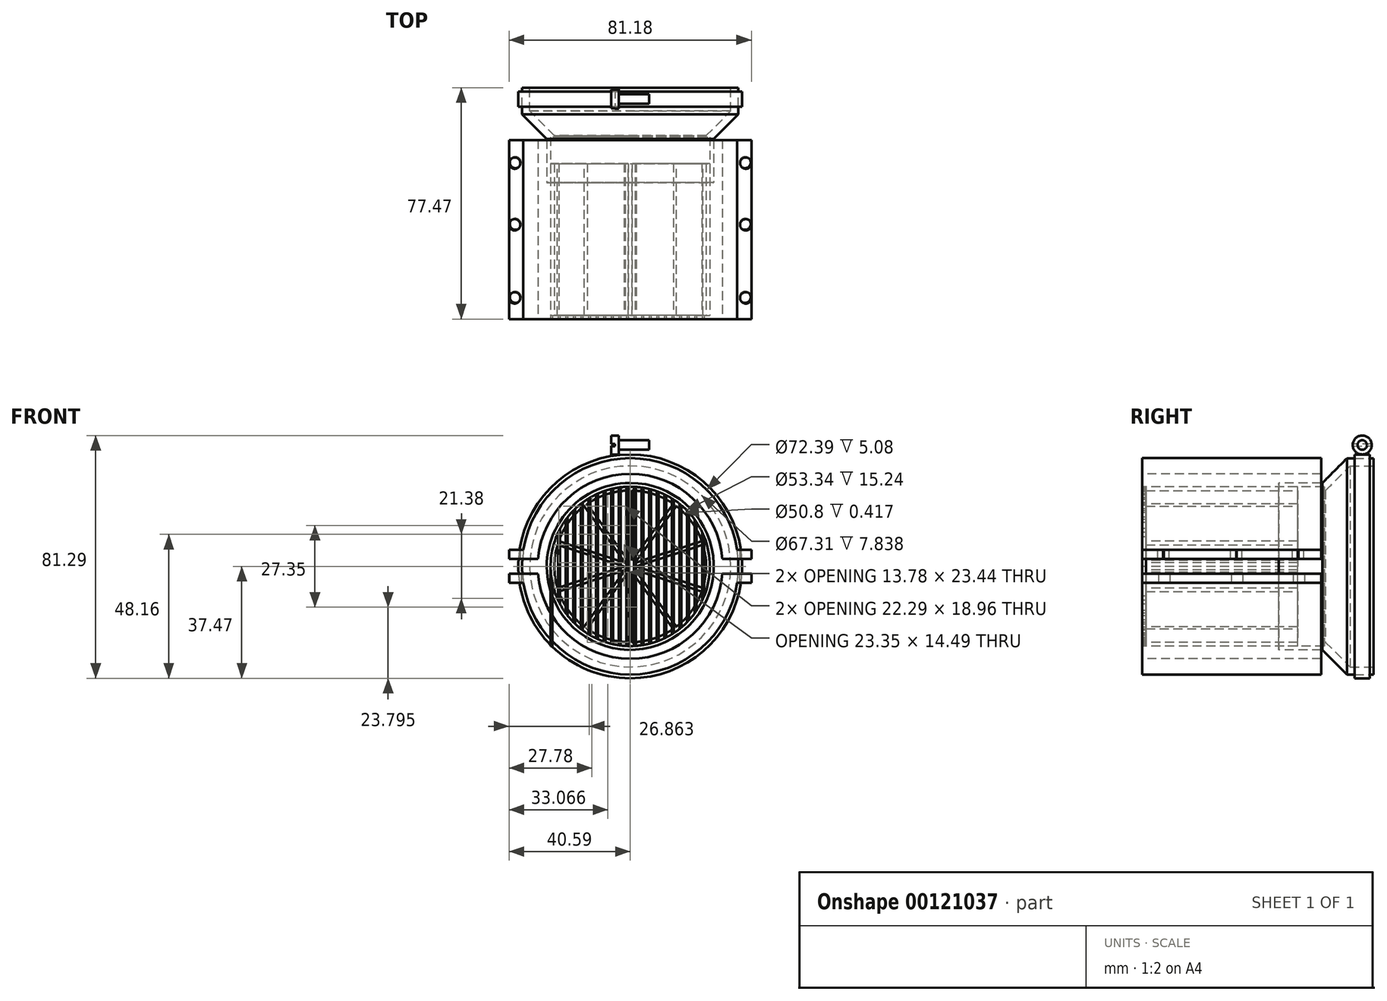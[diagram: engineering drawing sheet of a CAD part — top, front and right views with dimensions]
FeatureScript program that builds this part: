
annotation { "Feature Type Name" : "Feature", "Feature Type Description" : "" }
export const myFeature = defineFeature(function(context is Context, id is Id, definition is map)
    precondition{}
    {
        {
            var Q0;
            Q0=qCreatedBy(makeId("Front.planeOp"),FACE);
            var sketch = newSketch(context, id + "F0", { "sketchPlane" : qUnion([Q0])});
            skPoint(sketch, "E0", {"position": v(0.63, 25.4) * mm});
            skPoint(sketch, "E1", {"position": v(-0.64, 25.4) * mm});
            skLineSegment(sketch, "E2", {"start": v(-0.64, 25.4) * mm, "end": v(0.63, 25.4) * mm});
            skLineSegment(sketch, "E3", {"start": v(0.63, 25.4) * mm, "end": v(0.63, 0.46) * mm});
            skLineSegment(sketch, "E4", {"start": v(-0.64, 25.4) * mm, "end": v(-0.64, 0.2) * mm});
            skPoint(sketch, "E5.1.0", {"position": v(-14.42, 20.92) * mm});
            skLineSegment(sketch, "E5.1.1", {"start": v(-14.42, 20.92) * mm, "end": v(-0.64, 1.95) * mm});
            skLineSegment(sketch, "E5.1.2", {"start": v(-15.44, 20.18) * mm, "end": v(-1.66, 1.2) * mm});
            skPoint(sketch, "E5.1.3", {"position": v(-15.44, 20.18) * mm});
            skLineSegment(sketch, "E5.1.4", {"start": v(-15.44, 20.18) * mm, "end": v(-14.42, 20.92) * mm});
            skPoint(sketch, "E5.2.0", {"position": v(-23.96, 8.45) * mm});
            skLineSegment(sketch, "E5.2.1", {"start": v(-23.96, 8.45) * mm, "end": v(-1.66, 1.2) * mm});
            skLineSegment(sketch, "E5.2.2", {"start": v(-24.35, 7.25) * mm, "end": v(-2.05, 0) * mm});
            skPoint(sketch, "E5.2.3", {"position": v(-24.35, 7.25) * mm});
            skLineSegment(sketch, "E5.2.4", {"start": v(-24.35, 7.25) * mm, "end": v(-23.96, 8.45) * mm});
            skPoint(sketch, "E5.3.0", {"position": v(-24.35, -7.25) * mm});
            skLineSegment(sketch, "E5.3.1", {"start": v(-24.35, -7.25) * mm, "end": v(-2.05, 0) * mm});
            skLineSegment(sketch, "E5.3.2", {"start": v(-23.96, -8.45) * mm, "end": v(-1.66, -1.2) * mm});
            skPoint(sketch, "E5.3.3", {"position": v(-23.96, -8.45) * mm});
            skLineSegment(sketch, "E5.3.4", {"start": v(-23.96, -8.45) * mm, "end": v(-24.35, -7.25) * mm});
            skPoint(sketch, "E5.4.0", {"position": v(-15.44, -20.18) * mm});
            skLineSegment(sketch, "E5.4.1", {"start": v(-15.44, -20.18) * mm, "end": v(-1.66, -1.2) * mm});
            skLineSegment(sketch, "E5.4.2", {"start": v(-14.42, -20.92) * mm, "end": v(-0.63, -1.95) * mm});
            skPoint(sketch, "E5.4.3", {"position": v(-14.42, -20.92) * mm});
            skLineSegment(sketch, "E5.4.4", {"start": v(-14.42, -20.92) * mm, "end": v(-15.44, -20.18) * mm});
            skPoint(sketch, "E5.5.0", {"position": v(-0.64, -25.4) * mm});
            skLineSegment(sketch, "E5.5.1", {"start": v(-0.64, -25.4) * mm, "end": v(-0.63, -1.95) * mm});
            skLineSegment(sketch, "E5.5.2", {"start": v(0.63, -25.4) * mm, "end": v(0.64, -1.95) * mm});
            skPoint(sketch, "E5.5.3", {"position": v(0.63, -25.4) * mm});
            skLineSegment(sketch, "E5.5.4", {"start": v(0.63, -25.4) * mm, "end": v(-0.64, -25.4) * mm});
            skPoint(sketch, "E5.6.0", {"position": v(14.42, -20.92) * mm});
            skLineSegment(sketch, "E5.6.1", {"start": v(14.42, -20.92) * mm, "end": v(0.63, -1.95) * mm});
            skLineSegment(sketch, "E5.6.2", {"start": v(15.44, -20.18) * mm, "end": v(1.66, -1.2) * mm});
            skPoint(sketch, "E5.6.3", {"position": v(15.44, -20.18) * mm});
            skLineSegment(sketch, "E5.6.4", {"start": v(15.44, -20.18) * mm, "end": v(14.42, -20.92) * mm});
            skPoint(sketch, "E5.7.0", {"position": v(23.96, -8.45) * mm});
            skLineSegment(sketch, "E5.7.1", {"start": v(23.96, -8.45) * mm, "end": v(1.66, -1.2) * mm});
            skLineSegment(sketch, "E5.7.2", {"start": v(24.35, -7.25) * mm, "end": v(2.05, 0) * mm});
            skPoint(sketch, "E5.7.3", {"position": v(24.35, -7.25) * mm});
            skLineSegment(sketch, "E5.7.4", {"start": v(24.35, -7.25) * mm, "end": v(23.96, -8.45) * mm});
            skPoint(sketch, "E5.8.0", {"position": v(24.35, 7.25) * mm});
            skLineSegment(sketch, "E5.8.1", {"start": v(24.35, 7.25) * mm, "end": v(2.05, 0) * mm});
            skLineSegment(sketch, "E5.8.2", {"start": v(23.96, 8.45) * mm, "end": v(1.66, 1.2) * mm});
            skPoint(sketch, "E5.8.3", {"position": v(23.96, 8.45) * mm});
            skLineSegment(sketch, "E5.8.4", {"start": v(23.96, 8.45) * mm, "end": v(24.35, 7.25) * mm});
            skPoint(sketch, "E5.9.0", {"position": v(15.44, 20.18) * mm});
            skLineSegment(sketch, "E5.9.1", {"start": v(15.44, 20.18) * mm, "end": v(1.66, 1.2) * mm});
            skLineSegment(sketch, "E5.9.2", {"start": v(14.42, 20.92) * mm, "end": v(0.63, 1.95) * mm});
            skPoint(sketch, "E5.9.3", {"position": v(14.42, 20.92) * mm});
            skLineSegment(sketch, "E5.9.4", {"start": v(14.42, 20.92) * mm, "end": v(15.44, 20.18) * mm});
            skPoint(sketch, "E5.center", {"position": v(0, 0) * mm});
            skLineSegment(sketch, "E6.trimOffspring", {"start": v(0.63, 0.87) * mm, "end": v(0.24, 0.75) * mm});
            skLineSegment(sketch, "E7.trimOffspring", {"start": v(1.03, 0.33) * mm, "end": v(0.78, 0) * mm});
            skLineSegment(sketch, "E8.trimOffspring", {"start": v(1.03, 0.33) * mm, "end": v(0.63, 0.46) * mm});
            skLineSegment(sketch, "E9.trimOffspring", {"start": v(1.03, -0.33) * mm, "end": v(0.64, -0.46) * mm});
            skLineSegment(sketch, "E10.trimOffspring", {"start": v(1.03, -0.33) * mm, "end": v(0.78, 0) * mm});
            skLineSegment(sketch, "E11.trimOffspring", {"start": v(0.64, -0.87) * mm, "end": v(0.24, -0.75) * mm});
            skLineSegment(sketch, "E12.trimOffspring", {"start": v(0.64, -0.87) * mm, "end": v(0.64, -0.46) * mm});
            skLineSegment(sketch, "E13.trimOffspring", {"start": v(0, -1.08) * mm, "end": v(-0.24, -0.75) * mm});
            skLineSegment(sketch, "E14.trimOffspring", {"start": v(0, -1.08) * mm, "end": v(0.24, -0.75) * mm});
            skLineSegment(sketch, "E15.trimOffspring", {"start": v(-0.63, -0.87) * mm, "end": v(-0.63, -0.46) * mm});
            skLineSegment(sketch, "E16.trimOffspring", {"start": v(-0.63, -0.87) * mm, "end": v(-0.24, -0.75) * mm});
            skLineSegment(sketch, "E17.trimOffspring", {"start": v(-1.03, -0.33) * mm, "end": v(-0.78, 0) * mm});
            skLineSegment(sketch, "E18.trimOffspring", {"start": v(-1.03, -0.33) * mm, "end": v(-0.63, -0.46) * mm});
            skLineSegment(sketch, "E19.trimOffspring", {"start": v(-1.03, 0.33) * mm, "end": v(-0.2, 0.6) * mm});
            skLineSegment(sketch, "E20.trimOffspring", {"start": v(-1.03, 0.33) * mm, "end": v(-0.78, 0) * mm});
            skPoint(sketch, "E21.orphan", {"position": v(-0.64, 0) * mm});
            skPoint(sketch, "E22.orphan", {"position": v(0.63, 0) * mm});
            skPoint(sketch, "E23.orphan", {"position": v(0.64, 0) * mm});
            skPoint(sketch, "E24.orphan", {"position": v(0.51, -0.37) * mm});
            skPoint(sketch, "E25.orphan", {"position": v(-0.2, -0.6) * mm});
            skPoint(sketch, "E26.orphan", {"position": v(0.2, -0.6) * mm});
            skPoint(sketch, "E27.orphan", {"position": v(0.51, 0.37) * mm});
            skPoint(sketch, "E28.orphan", {"position": v(-0.51, 0.37) * mm});
            skPoint(sketch, "E29.orphan", {"position": v(-0.51, -0.37) * mm});
            skPoint(sketch, "E30.orphan", {"position": v(-0.2, 0.6) * mm});
            skSolve(sketch);
        }
        {
            var Q0;
            {var subQ6=sQuery(id+"F0.wireOp",EDGE,"E2");Q0=makeQuery(id+"F0.imprint","IMPRINT",FACE,{"disambiguationData":[TD([[makeQuery(id+"F0.imprint","IMPRINT",EDGE,{"derivedFrom":subQ6}),-1.0]])]});}
            var Q1;
            {var subQ1=sQuery(id+"F0.wireOp",EDGE,"E5.1.1");Q1=makeQuery(id+"F0.imprint","IMPRINT",FACE,{"disambiguationData":[TD([[makeQuery(id+"F0.imprint","IMPRINT",EDGE,{"derivedFrom":subQ1}),-1.0]])]});}
            extrude(context, id + "F1", {"entities" : qUnion([Q0, Q1]), "oppositeDirection" : true, "depth" : 50.8 * mm});
        }
        {
            var Q0;
            Q0=qCreatedBy(makeId("Front.planeOp"),FACE);
            var sketch = newSketch(context, id + "F2", { "sketchPlane" : qUnion([Q0])});
            skCircle(sketch, "E31", {"center": v(0, 0) * mm, "radius": 25.4 * mm});
            skCircle(sketch, "E32", {"center": v(0, 0) * mm, "radius": 26.67 * mm});
            skSolve(sketch);
        }
        {
            var Q0;
            Q0=makeQuery(id+"F2.imprint","IMPRINT",FACE,{"disambiguationData":[TD([[makeQuery(id+"F2.imprint","IMPRINT",EDGE,{"derivedFrom":sQuery(id+"F2.wireOp",EDGE,"E31")}),-1.0]])]});
            extrude(context, id + "F3", {"entities" : qUnion([Q0]), "operationType" : NewBodyOperationType.ADD, "oppositeDirection" : true, "depth" : 50.8 * mm});
        }
        {
            var Q0;
            Q0=makeQuery(id+"F3.boolean.opBoolean","MERGE",FACE,{"derivedFrom":[makeQuery(id+"F1.opExtrude","CAP_FACE",FACE,{"disambiguationData":[OSD([sQuery(id+"F0.wireOp",EDGE,"E2"),sQuery(id+"F0.wireOp",EDGE,"E3"),sQuery(id+"F0.wireOp",EDGE,"E4"),sQuery(id+"F0.wireOp",EDGE,"E5.1.1"),sQuery(id+"F0.wireOp",EDGE,"E5.1.2"),sQuery(id+"F0.wireOp",EDGE,"E5.1.4"),sQuery(id+"F0.wireOp",EDGE,"E5.2.1"),sQuery(id+"F0.wireOp",EDGE,"E5.2.2"),sQuery(id+"F0.wireOp",EDGE,"E5.2.4"),sQuery(id+"F0.wireOp",EDGE,"E5.3.1"),sQuery(id+"F0.wireOp",EDGE,"E5.3.2"),sQuery(id+"F0.wireOp",EDGE,"E5.3.4"),sQuery(id+"F0.wireOp",EDGE,"E5.4.1"),sQuery(id+"F0.wireOp",EDGE,"E5.4.2"),sQuery(id+"F0.wireOp",EDGE,"E5.4.4"),sQuery(id+"F0.wireOp",EDGE,"E5.5.1"),sQuery(id+"F0.wireOp",EDGE,"E5.5.2"),sQuery(id+"F0.wireOp",EDGE,"E5.5.4"),sQuery(id+"F0.wireOp",EDGE,"E5.6.1"),sQuery(id+"F0.wireOp",EDGE,"E5.6.2"),sQuery(id+"F0.wireOp",EDGE,"E5.6.4"),sQuery(id+"F0.wireOp",EDGE,"E5.7.1"),sQuery(id+"F0.wireOp",EDGE,"E5.7.2"),sQuery(id+"F0.wireOp",EDGE,"E5.7.4"),sQuery(id+"F0.wireOp",EDGE,"E5.8.1"),sQuery(id+"F0.wireOp",EDGE,"E5.8.2"),sQuery(id+"F0.wireOp",EDGE,"E5.8.4"),sQuery(id+"F0.wireOp",EDGE,"E5.9.1"),sQuery(id+"F0.wireOp",EDGE,"E5.9.2"),sQuery(id+"F0.wireOp",EDGE,"E5.9.4")])],"isStart":false}),makeQuery(id+"F3.opExtrude","CAP_FACE",FACE,{"disambiguationData":[OSD([sQuery(id+"F2.wireOp",EDGE,"E31"),sQuery(id+"F2.wireOp",EDGE,"E32")])],"isStart":false})]});
            var sketch = newSketch(context, id + "F4", { "sketchPlane" : qUnion([Q0])});
            skCircle(sketch, "E33", {"center": v(0, 0) * mm, "radius": 26.67 * mm});
            skCircle(sketch, "E34", {"center": v(0, 0) * mm, "radius": 27.94 * mm});
            skSolve(sketch);
        }
        {
            var Q0;
            Q0=makeQuery(id+"F4.imprint","IMPRINT",FACE,{"disambiguationData":[TD([[makeQuery(id+"F4.imprint","IMPRINT",EDGE,{"derivedFrom":sQuery(id+"F4.wireOp",EDGE,"E33")}),-1.0]])]});
            cPlane(context, id + "F5", {"entities" : qUnion([Q0]), "cplaneType" : CPlaneType.OFFSET, "offset" : 25.4 * mm, "width" : 152.4 * mm, "height" : 152.4 * mm});
        }
        {
            var Q0;
            Q0=qCreatedBy(id+"F5.planeOp",FACE);
            var sketch = newSketch(context, id + "F6", { "sketchPlane" : qUnion([Q0])});
            skCircle(sketch, "E35", {"center": v(0, 0) * mm, "radius": 36.2 * mm});
            skSolve(sketch);
        }
        {
            var Q0;
            Q0=makeQuery(id+"F4.imprint","IMPRINT",FACE,{"disambiguationData":[TD([[makeQuery(id+"F4.imprint","IMPRINT",EDGE,{"derivedFrom":sQuery(id+"F4.wireOp",EDGE,"E33")}),1.0]])]});
            extrude(context, id + "F7", {"entities" : qUnion([Q0]), "endBound" : BoundingType.SYMMETRIC, "depth" : 12.7 * mm});
        }
        {
            var Q0;
            Q0=makeQuery(id+"F6.imprint","IMPRINT",FACE,{"disambiguationData":[TD([[makeQuery(id+"F6.imprint","IMPRINT",EDGE,{"derivedFrom":sQuery(id+"F6.wireOp",EDGE,"E35")}),1.0]])]});
            extrude(context, id + "F8", {"entities" : qUnion([Q0]), "operationType" : NewBodyOperationType.ADD, "oppositeDirection" : true, "depth" : 19.05 * mm});
        }
        {
            var Q0;
            Q0=makeQuery(id+"F8.opExtrude","CAP_EDGE",EDGE,{"disambiguationData":[OSD([sQuery(id+"F6.wireOp",EDGE,"E35")])],"isStart":false});
            chamfer(context, id + "F9", {"entities" : qUnion([Q0]), "width" : 10.16 * mm, "tangentPropagation" : true});
        }
        {
            var Q0;
            Q0=makeQuery(id+"F8.opExtrude","CAP_FACE",FACE,{"disambiguationData":[OSD([sQuery(id+"F6.wireOp",EDGE,"E35")])],"isStart":true});
            shell(context, id + "F10", {"entities" : qUnion([Q0]), "thickness" : 2.54 * mm});
        }
        {
            var Q0;
            Q0=makeQuery(id+"F6.imprint","IMPRINT",FACE,{"disambiguationData":[TD([[makeQuery(id+"F6.imprint","IMPRINT",EDGE,{"derivedFrom":sQuery(id+"F6.wireOp",EDGE,"E35")}),1.0]])]});
            cPlane(context, id + "F11", {"entities" : qUnion([Q0]), "cplaneType" : CPlaneType.OFFSET, "offset" : 16.5 * mm, "oppositeDirection" : true, "width" : 152.4 * mm, "height" : 152.4 * mm});
        }
        {
            var Q0;
            Q0=qCreatedBy(id+"F11.planeOp",FACE);
            var sketch = newSketch(context, id + "F12", { "sketchPlane" : qUnion([Q0])});
            skCircle(sketch, "E36", {"center": v(0, 0) * mm, "radius": 26.67 * mm});
            skSolve(sketch);
        }
        {
            var Q0;
            Q0 = qSketchRegion(id + "F12", true);
            extrude(context, id + "F13", {"entities" : qUnion([Q0]), "operationType" : NewBodyOperationType.REMOVE, "oppositeDirection" : true, "depth" : 2.54 * mm});
        }
        {
            var Q0;
            Q0=makeQuery(id+"F3.boolean.opBoolean","MERGE",FACE,{"derivedFrom":[makeQuery(id+"F1.opExtrude","CAP_FACE",FACE,{"disambiguationData":[OSD([sQuery(id+"F0.wireOp",EDGE,"E2"),sQuery(id+"F0.wireOp",EDGE,"E3"),sQuery(id+"F0.wireOp",EDGE,"E4"),sQuery(id+"F0.wireOp",EDGE,"E5.1.1"),sQuery(id+"F0.wireOp",EDGE,"E5.1.2"),sQuery(id+"F0.wireOp",EDGE,"E5.1.4"),sQuery(id+"F0.wireOp",EDGE,"E5.2.1"),sQuery(id+"F0.wireOp",EDGE,"E5.2.2"),sQuery(id+"F0.wireOp",EDGE,"E5.2.4"),sQuery(id+"F0.wireOp",EDGE,"E5.3.1"),sQuery(id+"F0.wireOp",EDGE,"E5.3.2"),sQuery(id+"F0.wireOp",EDGE,"E5.3.4"),sQuery(id+"F0.wireOp",EDGE,"E5.4.1"),sQuery(id+"F0.wireOp",EDGE,"E5.4.2"),sQuery(id+"F0.wireOp",EDGE,"E5.4.4"),sQuery(id+"F0.wireOp",EDGE,"E5.5.1"),sQuery(id+"F0.wireOp",EDGE,"E5.5.2"),sQuery(id+"F0.wireOp",EDGE,"E5.5.4"),sQuery(id+"F0.wireOp",EDGE,"E5.6.1"),sQuery(id+"F0.wireOp",EDGE,"E5.6.2"),sQuery(id+"F0.wireOp",EDGE,"E5.6.4"),sQuery(id+"F0.wireOp",EDGE,"E5.7.1"),sQuery(id+"F0.wireOp",EDGE,"E5.7.2"),sQuery(id+"F0.wireOp",EDGE,"E5.7.4"),sQuery(id+"F0.wireOp",EDGE,"E5.8.1"),sQuery(id+"F0.wireOp",EDGE,"E5.8.2"),sQuery(id+"F0.wireOp",EDGE,"E5.8.4"),sQuery(id+"F0.wireOp",EDGE,"E5.9.1"),sQuery(id+"F0.wireOp",EDGE,"E5.9.2"),sQuery(id+"F0.wireOp",EDGE,"E5.9.4")])],"isStart":true}),makeQuery(id+"F3.opExtrude","CAP_FACE",FACE,{"disambiguationData":[OSD([sQuery(id+"F2.wireOp",EDGE,"E31"),sQuery(id+"F2.wireOp",EDGE,"E32")])],"isStart":true})]});
            cPlane(context, id + "F14", {"entities" : qUnion([Q0]), "cplaneType" : CPlaneType.OFFSET, "offset" : 1.27 * mm, "width" : 152.4 * mm, "height" : 152.4 * mm});
        }
        {
            var Q0;
            Q0=qCreatedBy(id+"F14.planeOp",FACE);
            var sketch = newSketch(context, id + "F15", { "sketchPlane" : qUnion([Q0])});
            skLineSegment(sketch, "E37.bottom", {"start": v(-26.67, 26.67) * mm, "end": v(26.67, 26.67) * mm});
            skLineSegment(sketch, "E37.top", {"start": v(-26.67, -26.67) * mm, "end": v(26.67, -26.67) * mm});
            skLineSegment(sketch, "E37.left", {"start": v(-26.67, 26.67) * mm, "end": v(-26.67, -26.67) * mm});
            skLineSegment(sketch, "E37.right", {"start": v(26.67, 26.67) * mm, "end": v(26.67, -26.67) * mm});
            skPoint(sketch, "E37.middle", {"position": v(0, 0) * mm});
            skPoint(sketch, "E38", {"position": v(-26.03, 26.67) * mm});
            skLineSegment(sketch, "E39", {"start": v(-26.03, 26.67) * mm, "end": v(-26.04, -26.67) * mm});
            skLineSegment(sketch, "E40.MirrorCS", {"start": v(-25.4, 26.67) * mm, "end": v(-25.4, -26.67) * mm});
            skLineSegment(sketch, "E41.MirrorCS", {"start": v(-24.77, 26.67) * mm, "end": v(-24.77, -26.67) * mm});
            skLineSegment(sketch, "E42.MirrorCS", {"start": v(-24.13, 26.67) * mm, "end": v(-24.13, -26.67) * mm});
            skLineSegment(sketch, "E43.MirrorCS", {"start": v(-23.5, 26.67) * mm, "end": v(-23.5, -26.67) * mm});
            skLineSegment(sketch, "E44.MirrorCS", {"start": v(-22.86, 26.67) * mm, "end": v(-22.86, -26.67) * mm});
            skLineSegment(sketch, "E45.MirrorCS", {"start": v(-22.23, 26.67) * mm, "end": v(-22.23, -26.67) * mm});
            skLineSegment(sketch, "E46.MirrorCS", {"start": v(-21.59, 26.67) * mm, "end": v(-21.59, -26.67) * mm});
            skLineSegment(sketch, "E47.MirrorCS", {"start": v(-20.96, 26.67) * mm, "end": v(-20.96, -26.67) * mm});
            skLineSegment(sketch, "E48.MirrorCS", {"start": v(-20.32, 26.67) * mm, "end": v(-20.32, -26.67) * mm});
            skLineSegment(sketch, "E49.MirrorCS", {"start": v(-19.68, 26.67) * mm, "end": v(-19.69, -26.67) * mm});
            skLineSegment(sketch, "E50.MirrorCS", {"start": v(-19.05, 26.67) * mm, "end": v(-19.05, -26.67) * mm});
            skLineSegment(sketch, "E51.MirrorCS", {"start": v(-18.42, 26.67) * mm, "end": v(-18.42, -26.67) * mm});
            skLineSegment(sketch, "E52.MirrorCS", {"start": v(-17.78, 26.67) * mm, "end": v(-17.78, -26.67) * mm});
            skLineSegment(sketch, "E53.MirrorCS", {"start": v(-17.15, 26.67) * mm, "end": v(-17.15, -26.67) * mm});
            skLineSegment(sketch, "E54.MirrorCS", {"start": v(-16.5, 26.67) * mm, "end": v(-16.51, -26.67) * mm});
            skLineSegment(sketch, "E55.MirrorCS", {"start": v(-15.87, 26.67) * mm, "end": v(-15.88, -26.67) * mm});
            skLineSegment(sketch, "E56.MirrorCS", {"start": v(-15.24, 26.67) * mm, "end": v(-15.24, -26.67) * mm});
            skLineSegment(sketch, "E57.MirrorCS", {"start": v(-14.6, 26.67) * mm, "end": v(-14.6, -26.67) * mm});
            skLineSegment(sketch, "E58.MirrorCS", {"start": v(-13.33, 26.67) * mm, "end": v(-13.34, -26.67) * mm});
            skLineSegment(sketch, "E59.MirrorCS", {"start": v(-13.97, 26.67) * mm, "end": v(-13.97, -26.67) * mm});
            skLineSegment(sketch, "E60.MirrorCS", {"start": v(-12.7, 26.67) * mm, "end": v(-12.7, -26.67) * mm});
            skLineSegment(sketch, "E61.MirrorCS", {"start": v(-12.07, 26.67) * mm, "end": v(-12.07, -26.67) * mm});
            skLineSegment(sketch, "E62.MirrorCS", {"start": v(-11.43, 26.67) * mm, "end": v(-11.43, -26.67) * mm});
            skLineSegment(sketch, "E63.MirrorCS", {"start": v(-10.8, 26.67) * mm, "end": v(-10.8, -26.67) * mm});
            skLineSegment(sketch, "E64.MirrorCS", {"start": v(-10.16, 26.67) * mm, "end": v(-10.16, -26.67) * mm});
            skLineSegment(sketch, "E65.MirrorCS", {"start": v(-9.52, 26.67) * mm, "end": v(-9.52, -26.67) * mm});
            skLineSegment(sketch, "E66.MirrorCS", {"start": v(-8.9, 26.67) * mm, "end": v(-8.9, -26.67) * mm});
            skLineSegment(sketch, "E67.MirrorCS", {"start": v(-8.26, 26.67) * mm, "end": v(-8.26, -26.67) * mm});
            skLineSegment(sketch, "E68.MirrorCS", {"start": v(-6.98, 26.67) * mm, "end": v(-6.99, -26.67) * mm});
            skLineSegment(sketch, "E69.MirrorCS", {"start": v(-7.62, 26.67) * mm, "end": v(-7.62, -26.67) * mm});
            skLineSegment(sketch, "E70.MirrorCS", {"start": v(-6.35, 26.67) * mm, "end": v(-6.35, -26.67) * mm});
            skLineSegment(sketch, "E71.MirrorCS", {"start": v(-5.71, 26.67) * mm, "end": v(-5.71, -26.67) * mm});
            skLineSegment(sketch, "E72.MirrorCS", {"start": v(-5.08, 26.67) * mm, "end": v(-5.08, -26.67) * mm});
            skLineSegment(sketch, "E73.MirrorCS", {"start": v(-4.45, 26.67) * mm, "end": v(-4.45, -26.67) * mm});
            skLineSegment(sketch, "E74.MirrorCS", {"start": v(-3.81, 26.67) * mm, "end": v(-3.81, -26.67) * mm});
            skLineSegment(sketch, "E75.MirrorCS", {"start": v(-3.18, 26.67) * mm, "end": v(-3.18, -26.67) * mm});
            skLineSegment(sketch, "E76.MirrorCS", {"start": v(-2.54, 26.67) * mm, "end": v(-2.54, -26.67) * mm});
            skLineSegment(sketch, "E77.MirrorCS", {"start": v(-1.9, 26.67) * mm, "end": v(-1.9, -26.67) * mm});
            skLineSegment(sketch, "E78.MirrorCS", {"start": v(-1.27, 26.67) * mm, "end": v(-1.27, -26.67) * mm});
            skLineSegment(sketch, "E79.MirrorCS", {"start": v(-0.64, 26.67) * mm, "end": v(-0.64, -26.67) * mm});
            skLineSegment(sketch, "E80.MirrorCS", {"start": v(0, 26.67) * mm, "end": v(0, -26.67) * mm});
            skCircle(sketch, "E81", {"center": v(0, 0) * mm, "radius": 26.67 * mm});
            skSolve(sketch);
        }
        {
            var Q0;
            {var subQ0=sQuery(id+"F15.wireOp",EDGE,"E81");var subQ1=sQuery(id+"F15.wireOp",EDGE,"E39");var subQ2=makeQuery(id+"F15.imprint","INTERSECT",VERTEX,{"disambiguationData":[OD(0.0)],"derivedFrom":[subQ1,subQ0]});Q0=makeQuery(id+"F15.imprint","IMPRINT",FACE,{"disambiguationData":[TD([[makeQuery(id+"F15.imprint","IMPRINT",EDGE,{"disambiguationData":[TD([[subQ2,-1.0]])],"derivedFrom":subQ1}),-1.0]])]});}
            var Q1;
            {var subQ0=sQuery(id+"F15.wireOp",EDGE,"E81");var subQ1=sQuery(id+"F15.wireOp",EDGE,"E42.MirrorCS");var subQ2=makeQuery(id+"F15.imprint","INTERSECT",VERTEX,{"disambiguationData":[OD(0.0)],"derivedFrom":[subQ1,subQ0]});Q1=makeQuery(id+"F15.imprint","IMPRINT",FACE,{"disambiguationData":[TD([[makeQuery(id+"F15.imprint","IMPRINT",EDGE,{"disambiguationData":[TD([[subQ2,-1.0]])],"derivedFrom":subQ1}),1.0]])]});}
            var Q2;
            {var subQ0=sQuery(id+"F15.wireOp",EDGE,"E81");var subQ1=sQuery(id+"F15.wireOp",EDGE,"E46.MirrorCS");var subQ2=makeQuery(id+"F15.imprint","INTERSECT",VERTEX,{"disambiguationData":[OD(0.0)],"derivedFrom":[subQ1,subQ0]});Q2=makeQuery(id+"F15.imprint","IMPRINT",FACE,{"disambiguationData":[TD([[makeQuery(id+"F15.imprint","IMPRINT",EDGE,{"disambiguationData":[TD([[subQ2,-1.0]])],"derivedFrom":subQ1}),1.0]])]});}
            var Q3;
            {var subQ0=sQuery(id+"F15.wireOp",EDGE,"E81");var subQ1=sQuery(id+"F15.wireOp",EDGE,"E50.MirrorCS");var subQ2=makeQuery(id+"F15.imprint","INTERSECT",VERTEX,{"disambiguationData":[OD(0.0)],"derivedFrom":[subQ1,subQ0]});Q3=makeQuery(id+"F15.imprint","IMPRINT",FACE,{"disambiguationData":[TD([[makeQuery(id+"F15.imprint","IMPRINT",EDGE,{"disambiguationData":[TD([[subQ2,-1.0]])],"derivedFrom":subQ1}),1.0]])]});}
            var Q4;
            {var subQ0=sQuery(id+"F15.wireOp",EDGE,"E81");var subQ1=sQuery(id+"F15.wireOp",EDGE,"E54.MirrorCS");var subQ2=makeQuery(id+"F15.imprint","INTERSECT",VERTEX,{"disambiguationData":[OD(0.0)],"derivedFrom":[subQ1,subQ0]});Q4=makeQuery(id+"F15.imprint","IMPRINT",FACE,{"disambiguationData":[TD([[makeQuery(id+"F15.imprint","IMPRINT",EDGE,{"disambiguationData":[TD([[subQ2,-1.0]])],"derivedFrom":subQ1}),1.0]])]});}
            var Q5;
            {var subQ0=sQuery(id+"F15.wireOp",EDGE,"E81");var subQ1=sQuery(id+"F15.wireOp",EDGE,"E58.MirrorCS");var subQ2=makeQuery(id+"F15.imprint","INTERSECT",VERTEX,{"disambiguationData":[OD(0.0)],"derivedFrom":[subQ1,subQ0]});Q5=makeQuery(id+"F15.imprint","IMPRINT",FACE,{"disambiguationData":[TD([[makeQuery(id+"F15.imprint","IMPRINT",EDGE,{"disambiguationData":[TD([[subQ2,-1.0]])],"derivedFrom":subQ1}),-1.0]])]});}
            var Q6;
            {var subQ0=sQuery(id+"F15.wireOp",EDGE,"E81");var subQ1=sQuery(id+"F15.wireOp",EDGE,"E62.MirrorCS");var subQ2=makeQuery(id+"F15.imprint","INTERSECT",VERTEX,{"disambiguationData":[OD(0.0)],"derivedFrom":[subQ1,subQ0]});Q6=makeQuery(id+"F15.imprint","IMPRINT",FACE,{"disambiguationData":[TD([[makeQuery(id+"F15.imprint","IMPRINT",EDGE,{"disambiguationData":[TD([[subQ2,-1.0]])],"derivedFrom":subQ1}),1.0]])]});}
            var Q7;
            {var subQ0=sQuery(id+"F15.wireOp",EDGE,"E81");var subQ1=sQuery(id+"F15.wireOp",EDGE,"E66.MirrorCS");var subQ2=makeQuery(id+"F15.imprint","INTERSECT",VERTEX,{"disambiguationData":[OD(0.0)],"derivedFrom":[subQ1,subQ0]});Q7=makeQuery(id+"F15.imprint","IMPRINT",FACE,{"disambiguationData":[TD([[makeQuery(id+"F15.imprint","IMPRINT",EDGE,{"disambiguationData":[TD([[subQ2,-1.0]])],"derivedFrom":subQ1}),1.0]])]});}
            var Q8;
            {var subQ0=sQuery(id+"F15.wireOp",EDGE,"E81");var subQ1=sQuery(id+"F15.wireOp",EDGE,"E70.MirrorCS");var subQ2=makeQuery(id+"F15.imprint","INTERSECT",VERTEX,{"disambiguationData":[OD(0.0)],"derivedFrom":[subQ1,subQ0]});Q8=makeQuery(id+"F15.imprint","IMPRINT",FACE,{"disambiguationData":[TD([[makeQuery(id+"F15.imprint","IMPRINT",EDGE,{"disambiguationData":[TD([[subQ2,-1.0]])],"derivedFrom":subQ1}),1.0]])]});}
            var Q9;
            {var subQ0=sQuery(id+"F15.wireOp",EDGE,"E81");var subQ1=sQuery(id+"F15.wireOp",EDGE,"E74.MirrorCS");var subQ2=makeQuery(id+"F15.imprint","INTERSECT",VERTEX,{"disambiguationData":[OD(0.0)],"derivedFrom":[subQ1,subQ0]});Q9=makeQuery(id+"F15.imprint","IMPRINT",FACE,{"disambiguationData":[TD([[makeQuery(id+"F15.imprint","IMPRINT",EDGE,{"disambiguationData":[TD([[subQ2,-1.0]])],"derivedFrom":subQ1}),1.0]])]});}
            var Q10;
            {var subQ0=sQuery(id+"F15.wireOp",EDGE,"E81");var subQ1=sQuery(id+"F15.wireOp",EDGE,"E79.MirrorCS");var subQ2=makeQuery(id+"F15.imprint","INTERSECT",VERTEX,{"disambiguationData":[OD(0.0)],"derivedFrom":[subQ1,subQ0]});Q10=makeQuery(id+"F15.imprint","IMPRINT",FACE,{"disambiguationData":[TD([[makeQuery(id+"F15.imprint","IMPRINT",EDGE,{"disambiguationData":[TD([[subQ2,-1.0]])],"derivedFrom":subQ1}),-1.0]])]});}
            extrude(context, id + "F16", {"entities" : qUnion([Q0, Q1, Q2, Q3, Q4, Q5, Q6, Q7, Q8, Q9, Q10]), "oppositeDirection" : true, "depth" : 1.27 * mm});
        }
        {
            var Q0;
            Q0=qCreatedBy(id+"F14.planeOp",FACE);
            var sketch = newSketch(context, id + "F17", { "sketchPlane" : qUnion([Q0])});
            skLineSegment(sketch, "E82.bottom", {"start": v(-26.67, 26.67) * mm, "end": v(26.67, 26.67) * mm});
            skLineSegment(sketch, "E82.top", {"start": v(-26.67, -26.67) * mm, "end": v(26.67, -26.67) * mm});
            skLineSegment(sketch, "E82.left", {"start": v(-26.67, 26.67) * mm, "end": v(-26.67, -26.67) * mm});
            skLineSegment(sketch, "E82.right", {"start": v(26.67, 26.67) * mm, "end": v(26.67, -26.67) * mm});
            skPoint(sketch, "E82.middle", {"position": v(0, 0) * mm});
            skCircle(sketch, "E83", {"center": v(0, 0) * mm, "radius": 26.67 * mm});
            skPoint(sketch, "E84", {"position": v(0.63, 26.67) * mm});
            skLineSegment(sketch, "E85", {"start": v(0, 26.67) * mm, "end": v(0, -26.67) * mm});
            skLineSegment(sketch, "E86", {"start": v(0.63, 26.67) * mm, "end": v(0.63, -26.67) * mm});
            skLineSegment(sketch, "E87.MirrorCS", {"start": v(1.27, 26.67) * mm, "end": v(1.27, -26.67) * mm});
            skLineSegment(sketch, "E88.MirrorCS", {"start": v(1.9, 26.67) * mm, "end": v(1.9, -26.67) * mm});
            skLineSegment(sketch, "E89.MirrorCS", {"start": v(2.54, 26.67) * mm, "end": v(2.54, -26.67) * mm});
            skLineSegment(sketch, "E90.MirrorCS", {"start": v(3.17, 26.67) * mm, "end": v(3.17, -26.67) * mm});
            skLineSegment(sketch, "E91.MirrorCS", {"start": v(3.8, 26.67) * mm, "end": v(3.8, -26.67) * mm});
            skLineSegment(sketch, "E92.MirrorCS", {"start": v(4.44, 26.67) * mm, "end": v(4.44, -26.67) * mm});
            skLineSegment(sketch, "E93.MirrorCS", {"start": v(5.08, 26.67) * mm, "end": v(5.08, -26.67) * mm});
            skLineSegment(sketch, "E94.MirrorCS", {"start": v(5.71, 26.67) * mm, "end": v(5.71, -26.67) * mm});
            skLineSegment(sketch, "E95.MirrorCS", {"start": v(6.35, 26.67) * mm, "end": v(6.35, -26.67) * mm});
            skLineSegment(sketch, "E96.MirrorCS", {"start": v(6.98, 26.67) * mm, "end": v(6.98, -26.67) * mm});
            skLineSegment(sketch, "E97.MirrorCS", {"start": v(7.62, 26.67) * mm, "end": v(7.62, -26.67) * mm});
            skLineSegment(sketch, "E98.MirrorCS", {"start": v(8.25, 26.67) * mm, "end": v(8.25, -26.67) * mm});
            skLineSegment(sketch, "E99.MirrorCS", {"start": v(8.89, 26.67) * mm, "end": v(8.89, -26.67) * mm});
            skLineSegment(sketch, "E100.MirrorCS", {"start": v(9.53, 26.67) * mm, "end": v(9.52, -26.67) * mm});
            skLineSegment(sketch, "E101.MirrorCS", {"start": v(10.16, 26.67) * mm, "end": v(10.16, -26.67) * mm});
            skLineSegment(sketch, "E102.MirrorCS", {"start": v(10.8, 26.67) * mm, "end": v(10.8, -26.67) * mm});
            skLineSegment(sketch, "E103.MirrorCS", {"start": v(12.06, 26.67) * mm, "end": v(12.06, -26.67) * mm});
            skLineSegment(sketch, "E104.MirrorCS", {"start": v(12.7, 26.67) * mm, "end": v(12.7, -26.67) * mm});
            skLineSegment(sketch, "E105.MirrorCS", {"start": v(11.43, 26.67) * mm, "end": v(11.43, -26.67) * mm});
            skLineSegment(sketch, "E106.MirrorCS", {"start": v(13.33, 26.67) * mm, "end": v(13.33, -26.67) * mm});
            skLineSegment(sketch, "E107.MirrorCS", {"start": v(13.97, 26.67) * mm, "end": v(13.97, -26.67) * mm});
            skLineSegment(sketch, "E108.MirrorCS", {"start": v(14.6, 26.67) * mm, "end": v(14.6, -26.67) * mm});
            skLineSegment(sketch, "E109.MirrorCS", {"start": v(15.24, 26.67) * mm, "end": v(15.24, -26.67) * mm});
            skLineSegment(sketch, "E110.MirrorCS", {"start": v(15.87, 26.67) * mm, "end": v(15.87, -26.67) * mm});
            skLineSegment(sketch, "E111.MirrorCS", {"start": v(16.5, 26.67) * mm, "end": v(16.5, -26.67) * mm});
            skLineSegment(sketch, "E112.MirrorCS", {"start": v(17.14, 26.67) * mm, "end": v(17.14, -26.67) * mm});
            skLineSegment(sketch, "E113.MirrorCS", {"start": v(17.78, 26.67) * mm, "end": v(17.78, -26.67) * mm});
            skLineSegment(sketch, "E114.MirrorCS", {"start": v(18.41, 26.67) * mm, "end": v(18.41, -26.67) * mm});
            skLineSegment(sketch, "E115.MirrorCS", {"start": v(19.05, 26.67) * mm, "end": v(19.05, -26.67) * mm});
            skLineSegment(sketch, "E116.MirrorCS", {"start": v(19.68, 26.67) * mm, "end": v(19.68, -26.67) * mm});
            skLineSegment(sketch, "E117.MirrorCS", {"start": v(20.32, 26.67) * mm, "end": v(20.32, -26.67) * mm});
            skLineSegment(sketch, "E118.MirrorCS", {"start": v(20.95, 26.67) * mm, "end": v(20.95, -26.67) * mm});
            skLineSegment(sketch, "E119.MirrorCS", {"start": v(21.59, 26.67) * mm, "end": v(21.59, -26.67) * mm});
            skLineSegment(sketch, "E120.MirrorCS", {"start": v(22.22, 26.67) * mm, "end": v(22.22, -26.67) * mm});
            skLineSegment(sketch, "E121.MirrorCS", {"start": v(22.86, 26.67) * mm, "end": v(22.86, -26.67) * mm});
            skLineSegment(sketch, "E122.MirrorCS", {"start": v(23.5, 26.67) * mm, "end": v(23.5, -26.67) * mm});
            skLineSegment(sketch, "E123.MirrorCS", {"start": v(24.13, 26.67) * mm, "end": v(24.13, -26.67) * mm});
            skLineSegment(sketch, "E124.MirrorCS", {"start": v(24.77, 26.67) * mm, "end": v(24.77, -26.67) * mm});
            skLineSegment(sketch, "E125.MirrorCS", {"start": v(25.4, 26.67) * mm, "end": v(25.4, -26.67) * mm});
            skLineSegment(sketch, "E126.MirrorCS", {"start": v(26.03, 26.67) * mm, "end": v(26.03, -26.67) * mm});
            skSolve(sketch);
        }
        {
            var Q0;
            {var subQ0=sQuery(id+"F17.wireOp",EDGE,"E88.MirrorCS");var subQ1=sQuery(id+"F17.wireOp",EDGE,"E83");var subQ2=makeQuery(id+"F17.imprint","INTERSECT",VERTEX,{"disambiguationData":[OD(0.0)],"derivedFrom":[subQ1,subQ0]});Q0=makeQuery(id+"F17.imprint","IMPRINT",FACE,{"disambiguationData":[TD([[makeQuery(id+"F17.imprint","IMPRINT",EDGE,{"disambiguationData":[TD([[subQ2,-1.0]])],"derivedFrom":subQ1}),1.0]])]});}
            var Q1;
            {var subQ0=sQuery(id+"F17.wireOp",EDGE,"E92.MirrorCS");var subQ1=sQuery(id+"F17.wireOp",EDGE,"E83");var subQ2=makeQuery(id+"F17.imprint","INTERSECT",VERTEX,{"disambiguationData":[OD(0.0)],"derivedFrom":[subQ1,subQ0]});Q1=makeQuery(id+"F17.imprint","IMPRINT",FACE,{"disambiguationData":[TD([[makeQuery(id+"F17.imprint","IMPRINT",EDGE,{"disambiguationData":[TD([[subQ2,-1.0]])],"derivedFrom":subQ1}),1.0]])]});}
            var Q2;
            {var subQ0=sQuery(id+"F17.wireOp",EDGE,"E96.MirrorCS");var subQ1=sQuery(id+"F17.wireOp",EDGE,"E83");var subQ2=makeQuery(id+"F17.imprint","INTERSECT",VERTEX,{"disambiguationData":[OD(0.0)],"derivedFrom":[subQ1,subQ0]});Q2=makeQuery(id+"F17.imprint","IMPRINT",FACE,{"disambiguationData":[TD([[makeQuery(id+"F17.imprint","IMPRINT",EDGE,{"disambiguationData":[TD([[subQ2,-1.0]])],"derivedFrom":subQ1}),1.0]])]});}
            var Q3;
            {var subQ0=sQuery(id+"F17.wireOp",EDGE,"E100.MirrorCS");var subQ1=sQuery(id+"F17.wireOp",EDGE,"E83");var subQ2=makeQuery(id+"F17.imprint","INTERSECT",VERTEX,{"disambiguationData":[OD(0.0)],"derivedFrom":[subQ1,subQ0]});Q3=makeQuery(id+"F17.imprint","IMPRINT",FACE,{"disambiguationData":[TD([[makeQuery(id+"F17.imprint","IMPRINT",EDGE,{"disambiguationData":[TD([[subQ2,-1.0]])],"derivedFrom":subQ1}),1.0]])]});}
            var Q4;
            {var subQ0=sQuery(id+"F17.wireOp",EDGE,"E103.MirrorCS");var subQ1=sQuery(id+"F17.wireOp",EDGE,"E83");var subQ2=makeQuery(id+"F17.imprint","INTERSECT",VERTEX,{"disambiguationData":[OD(0.0)],"derivedFrom":[subQ1,subQ0]});Q4=makeQuery(id+"F17.imprint","IMPRINT",FACE,{"disambiguationData":[TD([[makeQuery(id+"F17.imprint","IMPRINT",EDGE,{"disambiguationData":[TD([[subQ2,-1.0]])],"derivedFrom":subQ1}),1.0]])]});}
            var Q5;
            {var subQ0=sQuery(id+"F17.wireOp",EDGE,"E108.MirrorCS");var subQ1=sQuery(id+"F17.wireOp",EDGE,"E83");var subQ2=makeQuery(id+"F17.imprint","INTERSECT",VERTEX,{"disambiguationData":[OD(0.0)],"derivedFrom":[subQ1,subQ0]});Q5=makeQuery(id+"F17.imprint","IMPRINT",FACE,{"disambiguationData":[TD([[makeQuery(id+"F17.imprint","IMPRINT",EDGE,{"disambiguationData":[TD([[subQ2,-1.0]])],"derivedFrom":subQ1}),1.0]])]});}
            var Q6;
            {var subQ0=sQuery(id+"F17.wireOp",EDGE,"E112.MirrorCS");var subQ1=sQuery(id+"F17.wireOp",EDGE,"E83");var subQ2=makeQuery(id+"F17.imprint","INTERSECT",VERTEX,{"disambiguationData":[OD(0.0)],"derivedFrom":[subQ1,subQ0]});Q6=makeQuery(id+"F17.imprint","IMPRINT",FACE,{"disambiguationData":[TD([[makeQuery(id+"F17.imprint","IMPRINT",EDGE,{"disambiguationData":[TD([[subQ2,-1.0]])],"derivedFrom":subQ1}),1.0]])]});}
            var Q7;
            {var subQ0=sQuery(id+"F17.wireOp",EDGE,"E116.MirrorCS");var subQ1=sQuery(id+"F17.wireOp",EDGE,"E83");var subQ2=makeQuery(id+"F17.imprint","INTERSECT",VERTEX,{"disambiguationData":[OD(0.0)],"derivedFrom":[subQ1,subQ0]});Q7=makeQuery(id+"F17.imprint","IMPRINT",FACE,{"disambiguationData":[TD([[makeQuery(id+"F17.imprint","IMPRINT",EDGE,{"disambiguationData":[TD([[subQ2,-1.0]])],"derivedFrom":subQ1}),1.0]])]});}
            var Q8;
            {var subQ0=sQuery(id+"F17.wireOp",EDGE,"E120.MirrorCS");var subQ1=sQuery(id+"F17.wireOp",EDGE,"E83");var subQ2=makeQuery(id+"F17.imprint","INTERSECT",VERTEX,{"disambiguationData":[OD(0.0)],"derivedFrom":[subQ1,subQ0]});Q8=makeQuery(id+"F17.imprint","IMPRINT",FACE,{"disambiguationData":[TD([[makeQuery(id+"F17.imprint","IMPRINT",EDGE,{"disambiguationData":[TD([[subQ2,-1.0]])],"derivedFrom":subQ1}),1.0]])]});}
            var Q9;
            {var subQ0=sQuery(id+"F17.wireOp",EDGE,"E124.MirrorCS");var subQ1=sQuery(id+"F17.wireOp",EDGE,"E83");var subQ2=makeQuery(id+"F17.imprint","INTERSECT",VERTEX,{"disambiguationData":[OD(0.0)],"derivedFrom":[subQ1,subQ0]});Q9=makeQuery(id+"F17.imprint","IMPRINT",FACE,{"disambiguationData":[TD([[makeQuery(id+"F17.imprint","IMPRINT",EDGE,{"disambiguationData":[TD([[subQ2,-1.0]])],"derivedFrom":subQ1}),1.0]])]});}
            extrude(context, id + "F18", {"entities" : qUnion([Q0, Q1, Q2, Q3, Q4, Q5, Q6, Q7, Q8, Q9]), "operationType" : NewBodyOperationType.ADD, "oppositeDirection" : true, "depth" : 1.27 * mm});
        }
        {
            var Q0;
            Q0=qCreatedBy(makeId("Front.planeOp"),FACE);
            cPlane(context, id + "F19", {"entities" : qUnion([Q0]), "cplaneType" : CPlaneType.OFFSET, "offset" : 74.93 * mm, "oppositeDirection" : true, "width" : 152.4 * mm, "height" : 152.4 * mm});
        }
        {
            var Q0;
            Q0=qCreatedBy(id+"F19.planeOp",FACE);
            var sketch = newSketch(context, id + "F20", { "sketchPlane" : qUnion([Q0])});
            skCircle(sketch, "E127", {"center": v(0, 0) * mm, "radius": 36.2 * mm});
            skCircle(sketch, "E128", {"center": v(0, 0) * mm, "radius": 37.47 * mm});
            skSolve(sketch);
        }
        {
            var Q0;
            Q0=makeQuery(id+"F20.imprint","IMPRINT",FACE,{"disambiguationData":[TD([[makeQuery(id+"F20.imprint","IMPRINT",EDGE,{"derivedFrom":sQuery(id+"F20.wireOp",EDGE,"E127")}),-1.0]])]});
            extrude(context, id + "F21", {"entities" : qUnion([Q0]), "depth" : 5.08 * mm});
        }
        {
            var Q0;
            Q0=qCreatedBy(makeId("Right.planeOp"),FACE);
            cPlane(context, id + "F22", {"entities" : qUnion([Q0]), "cplaneType" : CPlaneType.OFFSET, "offset" : 6.35 * mm, "oppositeDirection" : true, "width" : 152.4 * mm, "height" : 152.4 * mm});
        }
        {
            var Q0;
            Q0=qCreatedBy(id+"F22.planeOp",FACE);
            var sketch = newSketch(context, id + "F23", { "sketchPlane" : qUnion([Q0])});
            skCircle(sketch, "E129", {"center": v(72.4, 40.64) * mm, "radius": 3.18 * mm});
            skSolve(sketch);
        }
        {
            var Q0;
            Q0=makeQuery(id+"F23.imprint","IMPRINT",FACE,{"disambiguationData":[TD([[makeQuery(id+"F23.imprint","IMPRINT",EDGE,{"derivedFrom":sQuery(id+"F23.wireOp",EDGE,"E129")}),1.0]])]});
            extrude(context, id + "F24", {"entities" : qUnion([Q0]), "depth" : 12.7 * mm});
        }
        {
            var Q0;
            Q0=makeQuery(id+"F24.opExtrude","CAP_FACE",FACE,{"disambiguationData":[OSD([sQuery(id+"F23.wireOp",EDGE,"E129")])],"isStart":true});
            var sketch = newSketch(context, id + "F25", { "sketchPlane" : qUnion([Q0])});
            skPoint(sketch, "E130", {"position": v(-72.4, 40.64) * mm});
            skPoint(sketch, "E131", {"position": v(-72.4, 41.02) * mm});
            skPoint(sketch, "E132", {"position": v(-72.4, 40.26) * mm});
            skLineSegment(sketch, "E133", {"start": v(-72.4, 41.02) * mm, "end": v(-75.54, 41.02) * mm});
            skLineSegment(sketch, "E134", {"start": v(-75.54, 41.02) * mm, "end": v(-69.24, 41.02) * mm});
            skLineSegment(sketch, "E135", {"start": v(-69.24, 40.27) * mm, "end": v(-75.55, 40.39) * mm});
            skCircle(sketch, "E136", {"center": v(-72.4, 40.64) * mm, "radius": 3.18 * mm});
            skPoint(sketch, "E137.end.orphan", {"position": v(-68.51, 40.26) * mm});
            skSolve(sketch);
        }
        {
            var Q0;
            {var subQ3=sQuery(id+"F25.wireOp",EDGE,"E135");Q0=makeQuery(id+"F25.imprint","IMPRINT",FACE,{"disambiguationData":[TD([[makeQuery(id+"F25.imprint","IMPRINT",EDGE,{"derivedFrom":subQ3}),-1.0]])]});}
            extrude(context, id + "F26", {"entities" : qUnion([Q0]), "operationType" : NewBodyOperationType.REMOVE, "oppositeDirection" : true, "depth" : 1.27 * mm});
        }
        {
            var Q0;
            Q0=makeQuery(id+"F24.opExtrude","CAP_FACE",FACE,{"disambiguationData":[OSD([sQuery(id+"F23.wireOp",EDGE,"E129")])],"isStart":false});
            var sketch = newSketch(context, id + "F27", { "sketchPlane" : qUnion([Q0])});
            skCircle(sketch, "E138", {"center": v(72.4, 40.64) * mm, "radius": 3.17 * mm});
            skCircle(sketch, "E139", {"center": v(72.4, 40.64) * mm, "radius": 1.59 * mm});
            skSolve(sketch);
        }
        {
            var Q0;
            Q0=makeQuery(id+"F27.imprint","IMPRINT",FACE,{"disambiguationData":[TD([[makeQuery(id+"F27.imprint","IMPRINT",EDGE,{"derivedFrom":sQuery(id+"F27.wireOp",EDGE,"E138")}),1.0]])]});
            extrude(context, id + "F28", {"entities" : qUnion([Q0]), "operationType" : NewBodyOperationType.REMOVE, "oppositeDirection" : true, "depth" : 10.16 * mm});
        }
        {
            var Q0;
            Q0=qCreatedBy(id+"F14.planeOp",FACE);
            var sketch = newSketch(context, id + "F29", { "sketchPlane" : qUnion([Q0])});
            skArc(sketch, "E140", {"start": v(-30.85, -2.47) * mm, "mid": v(0, -30.95) * mm, "end": v(30.85, -2.47) * mm});
            skArc(sketch, "E141.trimOffspring", {"start": v(30.85, 2.47) * mm, "mid": v(0, 30.95) * mm, "end": v(-30.85, 2.47) * mm});
            skArc(sketch, "E142", {"start": v(-35.8, -5.53) * mm, "mid": v(0, -36.22) * mm, "end": v(35.8, -5.53) * mm});
            skLineSegment(sketch, "E143", {"start": v(-30.85, 2.47) * mm, "end": v(-40.6, 2.47) * mm});
            skLineSegment(sketch, "E144", {"start": v(-40.6, -2.47) * mm, "end": v(-30.85, -2.47) * mm});
            skLineSegment(sketch, "E145", {"start": v(-36.13, -2.47) * mm, "end": v(-40.6, -2.47) * mm});
            skLineSegment(sketch, "E146.MirrorCS", {"start": v(30.85, 2.47) * mm, "end": v(40.6, 2.47) * mm});
            skLineSegment(sketch, "E147.MirrorCS", {"start": v(40.6, -2.47) * mm, "end": v(30.85, -2.47) * mm});
            skArc(sketch, "E148.trimOffspring", {"start": v(35.8, 5.53) * mm, "mid": v(0, 36.22) * mm, "end": v(-35.8, 5.53) * mm});
            skLineSegment(sketch, "E149", {"start": v(-40.6, 2.47) * mm, "end": v(-40.6, 5.53) * mm});
            skLineSegment(sketch, "E150", {"start": v(-40.6, 5.53) * mm, "end": v(-35.8, 5.53) * mm});
            skLineSegment(sketch, "E151.MirrorCS", {"start": v(40.6, 5.53) * mm, "end": v(35.8, 5.53) * mm});
            skLineSegment(sketch, "E152.MirrorCS", {"start": v(-40.6, -5.53) * mm, "end": v(-35.8, -5.53) * mm});
            skLineSegment(sketch, "E153.MirrorCS", {"start": v(40.6, -5.53) * mm, "end": v(35.8, -5.53) * mm});
            skLineSegment(sketch, "E154", {"start": v(-40.6, -2.47) * mm, "end": v(-40.6, -5.53) * mm});
            skLineSegment(sketch, "E155", {"start": v(40.6, -5.53) * mm, "end": v(40.6, -2.47) * mm});
            skLineSegment(sketch, "E156", {"start": v(40.6, 2.47) * mm, "end": v(40.6, 5.53) * mm});
            skSolve(sketch);
        }
        {
            var Q0;
            Q0 = qSketchRegion(id + "F29", true);
            extrude(context, id + "F30", {"entities" : qUnion([Q0]), "oppositeDirection" : true, "depth" : 59.9 * mm});
        }
        {
            var Q0;
            Q0=makeQuery(id+"F30.opExtrude","SWEPT_FACE",FACE,{"disambiguationData":[OSD([sQuery(id+"F29.wireOp",EDGE,"E150")])]});
            var sketch = newSketch(context, id + "F31", { "sketchPlane" : qUnion([Q0])});
            skPoint(sketch, "E157", {"position": v(-38.69, 30.26) * mm});
            skPoint(sketch, "E158", {"position": v(-38.69, 5.8) * mm});
            skPoint(sketch, "E159", {"position": v(-38.69, 50.92) * mm});
            skPoint(sketch, "E160.MirrorP", {"position": v(38.69, 5.8) * mm});
            skPoint(sketch, "E161.MirrorP", {"position": v(38.69, 30.26) * mm});
            skPoint(sketch, "E162.MirrorP", {"position": v(38.69, 50.92) * mm});
            skSolve(sketch);
        }
        {
            var Q0;
            Q0=sQuery(id+"F31.wireOp",VERTEX,"E159");
            var Q1;
            Q1=sQuery(id+"F31.wireOp",VERTEX,"E157");
            var Q2;
            Q2=sQuery(id+"F31.wireOp",VERTEX,"E158");
            var Q3;
            Q3=sQuery(id+"F31.wireOp",VERTEX,"E160.MirrorP");
            var Q4;
            Q4=sQuery(id+"F31.wireOp",VERTEX,"E161.MirrorP");
            var Q5;
            Q5=sQuery(id+"F31.wireOp",VERTEX,"E162.MirrorP");
            var Q6;
            Q6=makeQuery(id+"F30.opExtrude","SWEPT_BODY",BODY,{"disambiguationData":[OSD([sQuery(id+"F29.wireOp",EDGE,"E141.trimOffspring"),sQuery(id+"F29.wireOp",EDGE,"E143"),sQuery(id+"F29.wireOp",EDGE,"E146.MirrorCS"),sQuery(id+"F29.wireOp",EDGE,"E148.trimOffspring"),sQuery(id+"F29.wireOp",EDGE,"E149"),sQuery(id+"F29.wireOp",EDGE,"E150"),sQuery(id+"F29.wireOp",EDGE,"E151.MirrorCS"),sQuery(id+"F29.wireOp",EDGE,"E156")])]});
            hole(context, id + "F32", {"style" : HoleStyle.SIMPLE, "endStyle" : HoleEndStyle.THROUGH, "holeDiameter" : 3.8 * mm, "locations" : qUnion([Q0, Q1, Q2, Q3, Q4, Q5]), "scope" : qUnion([Q6]), "isTappedThrough" : true});
        }
        {
            var Q0;
            Q0=makeQuery(id+"F30.opExtrude","SWEPT_FACE",FACE,{"disambiguationData":[OSD([sQuery(id+"F29.wireOp",EDGE,"E152.MirrorCS")])]});
            var sketch = newSketch(context, id + "F33", { "sketchPlane" : qUnion([Q0])});
            skPoint(sketch, "E163", {"position": v(-38.42, -51.14) * mm});
            skPoint(sketch, "E164.positionSnap0", {"position": v(-40.6, -28.69) * mm});
            skPoint(sketch, "E165", {"position": v(-38.42, -6.03) * mm});
            skPoint(sketch, "E166", {"position": v(-38.42, -30.49) * mm});
            skPoint(sketch, "E167.MirrorP", {"position": v(38.42, -6.03) * mm});
            skPoint(sketch, "E168.MirrorP", {"position": v(38.42, -30.49) * mm});
            skPoint(sketch, "E169.MirrorP", {"position": v(38.42, -51.14) * mm});
            skSolve(sketch);
        }
        {
            var Q0;
            Q0=sQuery(id+"F33.wireOp",VERTEX,"E166");
            var Q1;
            Q1=sQuery(id+"F33.wireOp",VERTEX,"E163");
            var Q2;
            Q2=sQuery(id+"F33.wireOp",VERTEX,"E165");
            var Q3;
            Q3=sQuery(id+"F33.wireOp",VERTEX,"E167.MirrorP");
            var Q4;
            Q4=sQuery(id+"F33.wireOp",VERTEX,"E168.MirrorP");
            var Q5;
            Q5=sQuery(id+"F33.wireOp",VERTEX,"E169.MirrorP");
            var Q6;
            Q6=makeQuery(id+"F30.opExtrude","SWEPT_BODY",BODY,{"disambiguationData":[OSD([sQuery(id+"F29.wireOp",EDGE,"E140"),sQuery(id+"F29.wireOp",EDGE,"E142"),sQuery(id+"F29.wireOp",EDGE,"E144"),sQuery(id+"F29.wireOp",EDGE,"E145"),sQuery(id+"F29.wireOp",EDGE,"E147.MirrorCS"),sQuery(id+"F29.wireOp",EDGE,"E152.MirrorCS"),sQuery(id+"F29.wireOp",EDGE,"E153.MirrorCS"),sQuery(id+"F29.wireOp",EDGE,"E154"),sQuery(id+"F29.wireOp",EDGE,"E155")])]});
            hole(context, id + "F34", {"style" : HoleStyle.SIMPLE, "endStyle" : HoleEndStyle.THROUGH, "holeDiameter" : 3.8 * mm, "locations" : qUnion([Q0, Q1, Q2, Q3, Q4, Q5]), "scope" : qUnion([Q6]), "isTappedThrough" : true});
        }
    });
